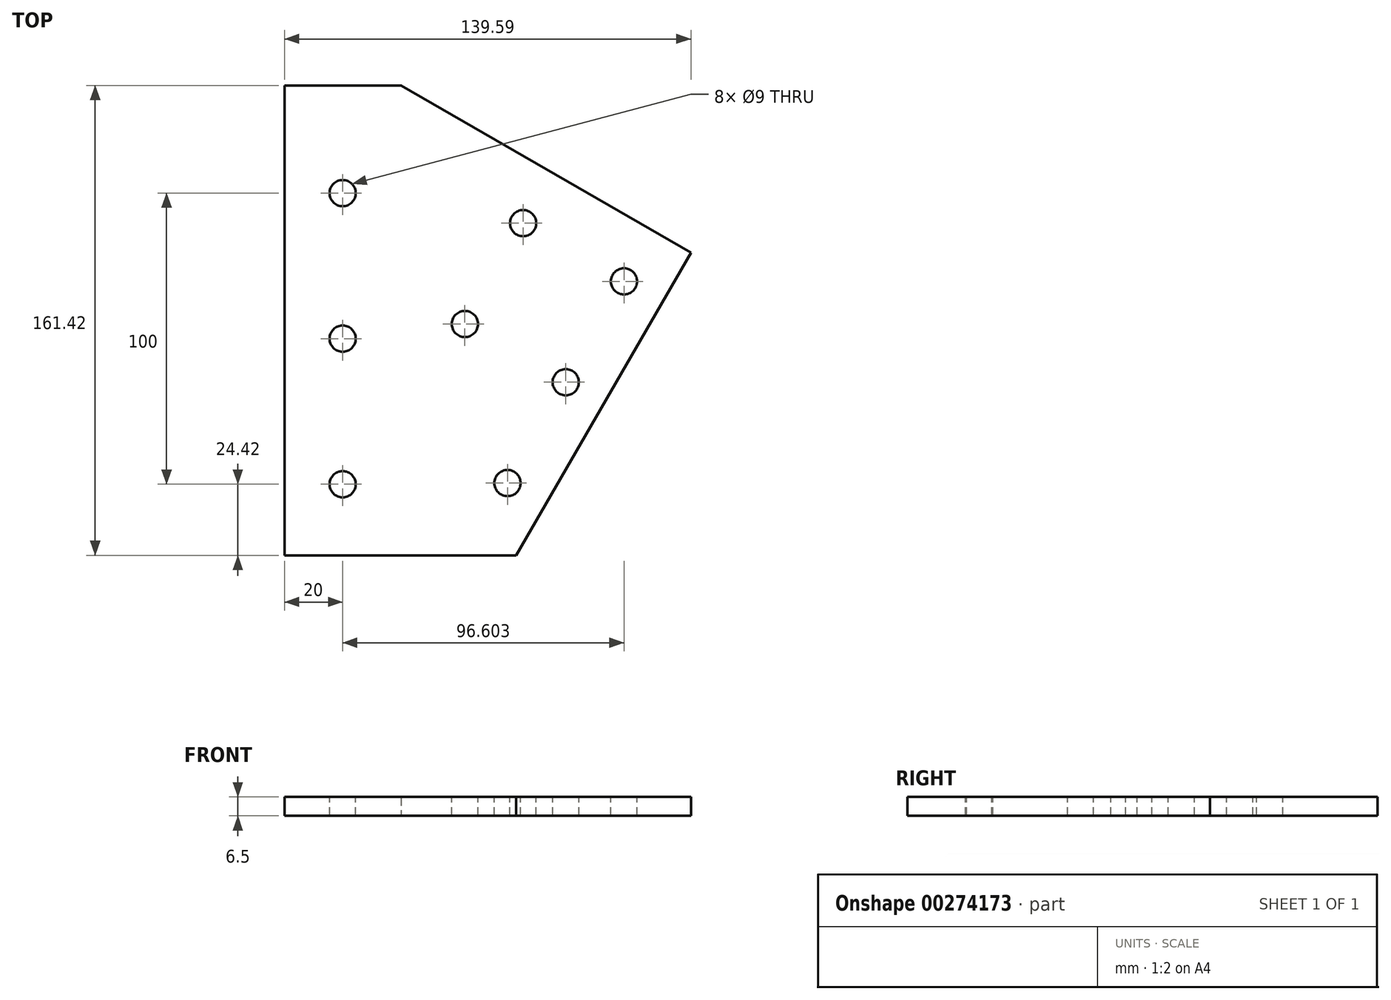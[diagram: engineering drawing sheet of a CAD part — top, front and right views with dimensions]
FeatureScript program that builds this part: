
annotation { "Feature Type Name" : "Feature", "Feature Type Description" : "" }
export const myFeature = defineFeature(function(context is Context, id is Id, definition is map)
    precondition{}
    {
        {
            var Q0;
            Q0=qCreatedBy(makeId("Top.planeOp"),FACE);
            var sketch = newSketch(context, id + "F0", { "sketchPlane" : qUnion([Q0])});
            skLineSegment(sketch, "E0", {"start": v(0, 200) * mm, "end": v(-40, 200) * mm});
            skLineSegment(sketch, "E1", {"start": v(-40, 200) * mm, "end": v(-40, 0) * mm});
            skLineSegment(sketch, "E2", {"start": v(-40, 0) * mm, "end": v(160, 0) * mm});
            skLineSegment(sketch, "E3", {"start": v(160, 0) * mm, "end": v(160, 107.62) * mm});
            skLineSegment(sketch, "E4", {"start": v(160, 107.62) * mm, "end": v(0, 200) * mm});
            skLineSegment(sketch, "E5", {"start": v(99.6, 142.5) * mm, "end": v(17.32, 0) * mm});
            skLineSegment(sketch, "E6", {"start": v(-40, 38.58) * mm, "end": v(39.6, 38.58) * mm});
            skSolve(sketch);
        }
        {
            var Q0;
            Q0=makeQuery(id+"F0.imprint","IMPRINT",FACE,{"disambiguationData":[TD([[makeQuery(id+"F0.imprint","IMPRINT",EDGE,{"derivedFrom":sQuery(id+"F0.wireOp",EDGE,"E0")}),1.0]])]});
            extrude(context, id + "F1", {"entities" : qUnion([Q0]), "depth" : 6.5 * mm});
        }
        {
            var Q0;
            Q0=makeQuery(id+"F1.opExtrude","CAP_FACE",FACE,{"disambiguationData":[OSD([sQuery(id+"F0.wireOp",EDGE,"E0"),sQuery(id+"F0.wireOp",EDGE,"E1"),sQuery(id+"F0.wireOp",EDGE,"E2"),sQuery(id+"F0.wireOp",EDGE,"E3"),sQuery(id+"F0.wireOp",EDGE,"E4")])],"isStart":false});
            var sketch = newSketch(context, id + "F2", { "sketchPlane" : qUnion([Q0])});
            skLineSegment(sketch, "E7", {"start": v(-20, 200) * mm, "end": v(-20, 0) * mm, "construction": true});
            skLineSegment(sketch, "E8.0", {"start": v(102.75, 117.58) * mm, "end": v(26.1, 161.83) * mm, "construction": true});
            skLineSegment(sketch, "E9", {"start": v(9.45, 125.26) * mm, "end": v(109.38, 67.57) * mm, "construction": true});
            skLineSegment(sketch, "E10", {"start": v(-7.12, 88.64) * mm, "end": v(80.33, 38.15) * mm, "construction": true});
            skLineSegment(sketch, "E11", {"start": v(1.96, 83.4) * mm, "end": v(41.96, 152.68) * mm, "construction": true});
            skLineSegment(sketch, "E12", {"start": v(36.6, 63.4) * mm, "end": v(76.6, 132.68) * mm, "construction": true});
            skPoint(sketch, "E13", {"position": v(-20, 163) * mm});
            skPoint(sketch, "E14", {"position": v(-20, 113) * mm});
            skPoint(sketch, "E15", {"position": v(-20, 63) * mm});
            skPoint(sketch, "E16", {"position": v(56.6, 98.04) * mm});
            skPoint(sketch, "E17", {"position": v(21.96, 118.04) * mm});
            skSolve(sketch);
        }
        {
            var Q0;
            Q0=sQuery(id+"F2.wireOp",VERTEX,"E13");
            var Q1;
            Q1=sQuery(id+"F2.wireOp",VERTEX,"E14");
            var Q2;
            Q2=sQuery(id+"F2.wireOp",VERTEX,"E15");
            var Q3;
            Q3=sQuery(id+"F2.wireOp",VERTEX,"E11.end");
            var Q4;
            Q4=sQuery(id+"F2.wireOp",VERTEX,"E12.end");
            var Q5;
            Q5=sQuery(id+"F2.wireOp",VERTEX,"E16");
            var Q6;
            Q6=sQuery(id+"F2.wireOp",VERTEX,"E12.start");
            var Q7;
            Q7=sQuery(id+"F2.wireOp",VERTEX,"E17");
            var Q8;
            Q8=makeQuery(id+"F1.opExtrude","SWEPT_BODY",BODY,{"disambiguationData":[OSD([sQuery(id+"F0.wireOp",EDGE,"E0"),sQuery(id+"F0.wireOp",EDGE,"E1"),sQuery(id+"F0.wireOp",EDGE,"E2"),sQuery(id+"F0.wireOp",EDGE,"E3"),sQuery(id+"F0.wireOp",EDGE,"E4")])]});
            hole(context, id + "F3", {"style" : HoleStyle.SIMPLE, "endStyle" : HoleEndStyle.THROUGH, "standardTappedOrClearance" : lookupTablePath({ "fit" : "Normal", "standard" : "ISO", "size" : "M8", "type" : "Clearance" }), "standardBlindInLast" : lookupTablePath({ "fit" : "Normal", "standard" : "ISO", "engagement" : "75%", "pitch" : "1.25 mm", "size" : "M8", "type" : "Clearance & tapped" }), "holeDiameter" : 9 * mm, "majorDiameter" : 5 * mm, "tappedDepth" : 12 * mm, "tapClearance" : 3, "locations" : qUnion([Q0, Q1, Q2, Q3, Q4, Q5, Q6, Q7]), "scope" : qUnion([Q8])});
        }
    });
